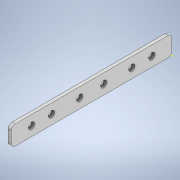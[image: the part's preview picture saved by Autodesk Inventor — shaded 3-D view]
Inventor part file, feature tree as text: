
AUTODESK INVENTOR PART (.ipt)
format: ipt  version: 2021 (Build 250183000, 183)  size: 134,144 bytes
history: native  units: mm
features: sketch x3, extrude x2, fillet x1
ambient origin geometry x8: Origin, YZ Plane, XZ Plane, XY Plane, X Axis, Y Axis, Z Axis, Center Point
bodies: Solid1 (feature_tree)
feature tree (6):
  extrude  "Extrusion1"  Depth=24.0mm
  fillet  "Fillet1"  Radius=200.0mm
  extrude  "Extrusion2"  Depth=5.0mm
  sketch  "Sketch3"  dims[d6=8.0mm d7=10.0mm d8=0.0mm d9=50.0mm d10=50.0mm d11=12.0mm d12=12.0mm d13=8.0mm d14=8.0mm d15=8.0mm d16=8.0mm d17=25.0mm d18=25.0mm d19=85.0mm d20=85.0mm]
  sketch  "Sketch1"  dims[d0=4.0mm d1=24.0mm d2=200.0mm d3=0.0mm]
  sketch  "Sketch2"  dims[d4=5.0mm d5=8.0mm]
